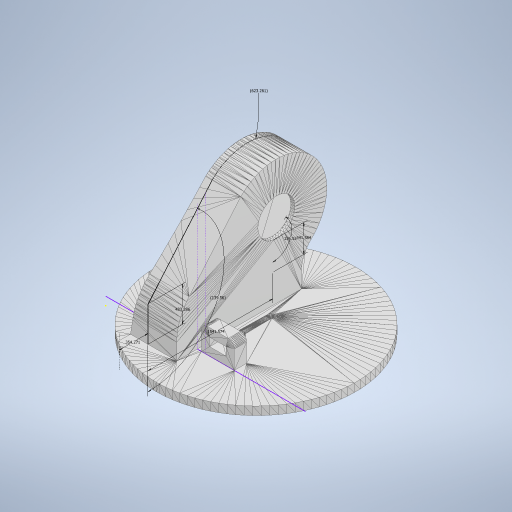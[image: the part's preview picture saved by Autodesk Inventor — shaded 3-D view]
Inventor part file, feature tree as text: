
AUTODESK INVENTOR PART (.ipt)
format: ipt  version: 2024.1 (Build 281209000, 209)  size: 296,960 bytes
history: native  units: in
note: dims shown in document units (in); Inventor stores cm internally (conversion verified against a paired STEP export)
features: other x2, sketch x2
ambient origin geometry x8: Origin, YZ Plane, XZ Plane, XY Plane, X Axis, Y Axis, Z Axis, Center Point
feature tree (4):
  other  "Waist"
  sketch  "Sketch1"  dims[d0=13.9477in]
  sketch  "Sketch2"  dims[d1=60.6919in d2=13.4482in d3=24.5379in d4=0.9589in d5=0.9382in d6=17.0585in]
  other  "MeshFeature1"
